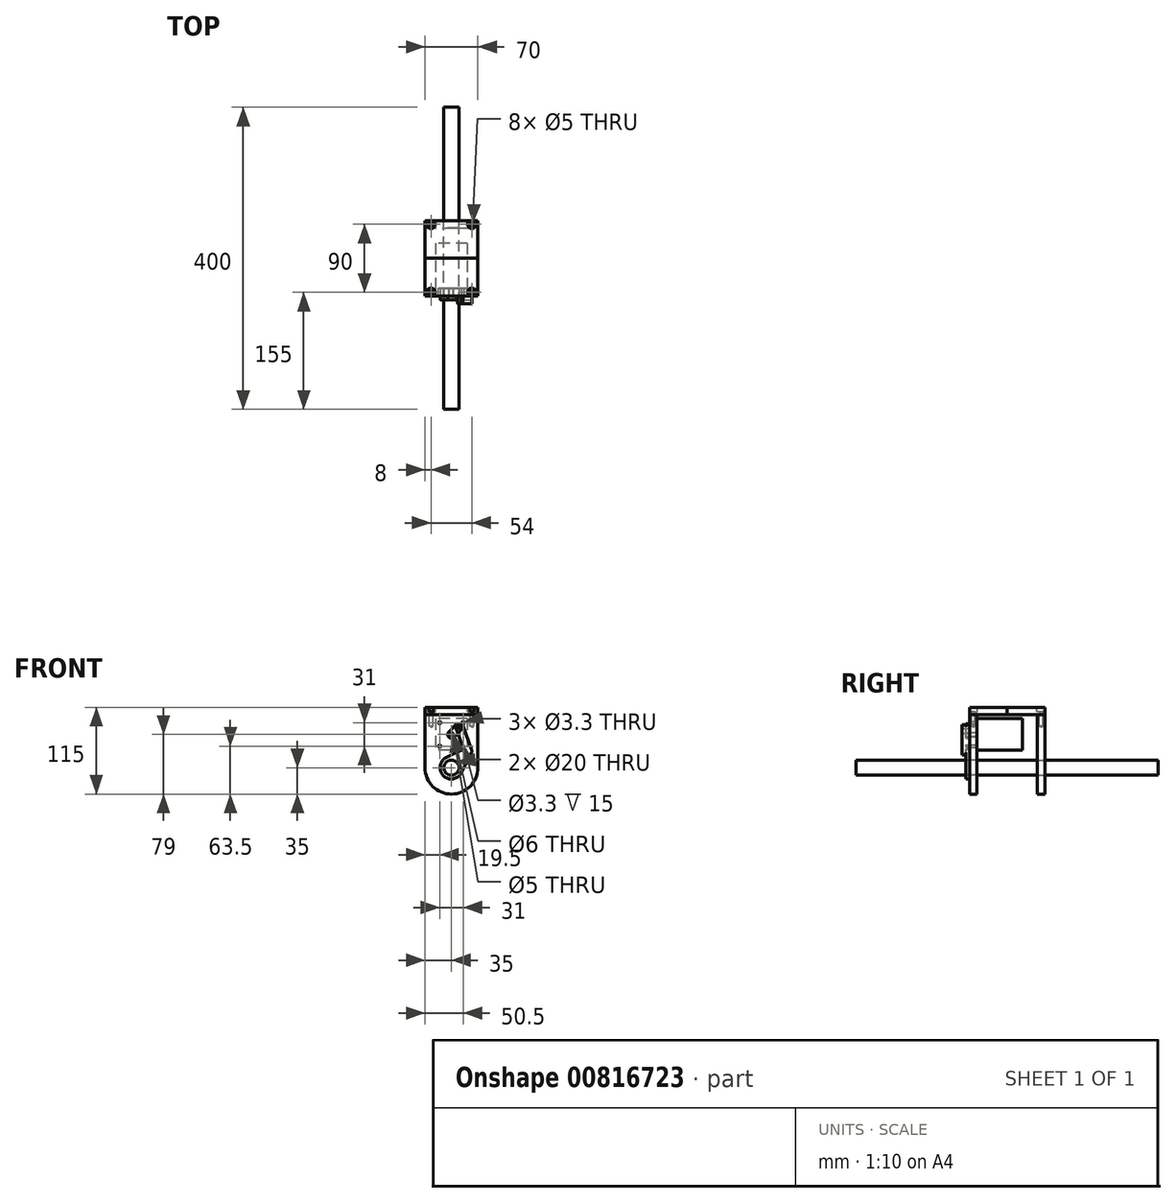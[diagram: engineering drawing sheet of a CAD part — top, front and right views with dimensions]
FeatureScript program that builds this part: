
annotation { "Feature Type Name" : "Feature", "Feature Type Description" : "" }
export const myFeature = defineFeature(function(context is Context, id is Id, definition is map)
    precondition{}
    {
        {
            var Q0;
            Q0=qCreatedBy(makeId("Front.planeOp"),FACE);
            var sketch = newSketch(context, id + "F0", { "sketchPlane" : qUnion([Q0])});
            skCircle(sketch, "E0", {"center": v(0, 0) * mm, "radius": 10 * mm});
            skLineSegment(sketch, "E1.bottom", {"start": v(-35, 70) * mm, "end": v(35, 70) * mm});
            skLineSegment(sketch, "E1.left", {"start": v(-35, 70) * mm, "end": v(-35, 0) * mm});
            skLineSegment(sketch, "E1.right", {"start": v(35, 70) * mm, "end": v(35, 0) * mm});
            skArc(sketch, "E2", {"start": v(-35, 0) * mm, "mid": v(0, -35) * mm, "end": v(35, 0) * mm});
            skSolve(sketch);
        }
        {
            var Q0;
            Q0=makeQuery(id+"F0.imprint","IMPRINT",FACE,{"disambiguationData":[TD([[makeQuery(id+"F0.imprint","IMPRINT",EDGE,{"derivedFrom":sQuery(id+"F0.wireOp",EDGE,"E0")}),1.0]])]});
            extrude(context, id + "F1", {"entities" : qUnion([Q0]), "depth" : 200 * mm, "offsetDistance" : 25 * mm, "hasSecondDirection" : true, "secondDirectionOppositeDirection" : true, "secondDirectionDepth" : 200 * mm});
        }
        {
            var Q0;
            Q0=makeQuery(id+"F0.imprint","IMPRINT",FACE,{"disambiguationData":[TD([[makeQuery(id+"F0.imprint","IMPRINT",EDGE,{"derivedFrom":sQuery(id+"F0.wireOp",EDGE,"E0")}),-1.0]])]});
            extrude(context, id + "F2", {"entities" : qUnion([Q0]), "depth" : 10 * mm, "offsetDistance" : 25 * mm});
        }
        {
            var Q0;
            Q0=makeQuery(id+"F2.opExtrude","SWEPT_BODY",BODY,{"disambiguationData":[OSD([sQuery(id+"F0.wireOp",EDGE,"E0"),sQuery(id+"F0.wireOp",EDGE,"E1.bottom"),sQuery(id+"F0.wireOp",EDGE,"E1.left"),sQuery(id+"F0.wireOp",EDGE,"E1.right"),sQuery(id+"F0.wireOp",EDGE,"E2")])]});
            var Q1;
            Q1=makeQuery(id+"F1.opExtrude","SWEPT_FACE",FACE,{"disambiguationData":[OSD([sQuery(id+"F0.wireOp",EDGE,"E0")])]});
            transform(context, id + "F3", {"entities" : qUnion([Q0]), "transformType" : TransformType.TRANSLATION_DISTANCE, "transformDirection" : qUnion([Q1]), "distance" : 50 * mm, "makeCopy" : false});
        }
        {
            var Q0;
            Q0=makeQuery(id+"F2.opExtrude","SWEPT_FACE",FACE,{"disambiguationData":[OSD([sQuery(id+"F0.wireOp",EDGE,"E1.bottom")])]});
            var sketch = newSketch(context, id + "F4", { "sketchPlane" : qUnion([Q0])});
            skPoint(sketch, "E3", {"position": v(27, 45) * mm});
            skPoint(sketch, "E3.positionSnap0", {"position": v(35, 45) * mm});
            skPoint(sketch, "E4", {"position": v(-27, 45) * mm});
            skPoint(sketch, "E4.positionSnap0", {"position": v(-35, 45) * mm});
            skSolve(sketch);
        }
        {
            var Q0;
            Q0=sQuery(id+"F4.wireOp",VERTEX,"E3");
            var Q1;
            Q1=sQuery(id+"F4.wireOp",VERTEX,"E4");
            var Q2;
            Q2=makeQuery(id+"F2.opExtrude","SWEPT_BODY",BODY,{"disambiguationData":[OSD([sQuery(id+"F0.wireOp",EDGE,"E0"),sQuery(id+"F0.wireOp",EDGE,"E1.bottom"),sQuery(id+"F0.wireOp",EDGE,"E1.left"),sQuery(id+"F0.wireOp",EDGE,"E1.right"),sQuery(id+"F0.wireOp",EDGE,"E2")])]});
            hole(context, id + "F5", {"style" : HoleStyle.SIMPLE, "endStyle" : HoleEndStyle.BLIND, "standardTappedOrClearance" : lookupTablePath({ "standard" : "ISO", "engagement" : "75%", "pitch" : "1 mm", "size" : "M6", "type" : "Tapped" }), "standardBlindInLast" : lookupTablePath({ "standard" : "ISO", "engagement" : "75%", "pitch" : "1 mm", "size" : "M6", "type" : "Tapped" }), "holeDiameter" : 5 * mm, "majorDiameter" : 6 * mm, "showTappedDepth" : true, "holeDepth" : 15 * mm, "isTappedThrough" : true, "tappedDepth" : 12 * mm, "tapClearance" : 3, "locations" : qUnion([Q0, Q1]), "scope" : qUnion([Q2])});
        }
        {
            var Q0;
            Q0=makeQuery(id+"F2.opExtrude","SWEPT_FACE",FACE,{"disambiguationData":[OSD([sQuery(id+"F0.wireOp",EDGE,"E1.bottom")])]});
            var sketch = newSketch(context, id + "F6", { "sketchPlane" : qUnion([Q0])});
            skLineSegment(sketch, "E5.bottom", {"start": v(-35, 50) * mm, "end": v(35, 50) * mm});
            skLineSegment(sketch, "E5.top", {"start": v(-35, 0) * mm, "end": v(35, 0) * mm});
            skLineSegment(sketch, "E5.left", {"start": v(-35, 50) * mm, "end": v(-35, 0) * mm});
            skLineSegment(sketch, "E5.right", {"start": v(35, 50) * mm, "end": v(35, 0) * mm});
            skPoint(sketch, "E6", {"position": v(0, 50) * mm});
            skPoint(sketch, "E7.centerSnap0", {"position": v(-35, 45) * mm});
            skPoint(sketch, "E8.centerSnap0", {"position": v(35, 45) * mm});
            skSolve(sketch);
        }
        {
            var Q0;
            {var subQ1=sQuery(id+"F0.wireOp",EDGE,"E1.bottom");Q0=makeQuery(id+"F6.imprint","IMPRINT",FACE,{"disambiguationData":[TD([[makeQuery(id+"F6.imprint","IMPRINT",EDGE,{"derivedFrom":makeQuery(id+"F2.opExtrude","CAP_EDGE",EDGE,{"disambiguationData":[OSD([subQ1])],"isStart":false})}),1.0]])]});}
            var Q1;
            Q1=makeQuery(id+"F6.imprint","IMPRINT",FACE,{"disambiguationData":[TD([[makeQuery(id+"F6.imprint","IMPRINT",EDGE,{"derivedFrom":sQuery(id+"F6.wireOp",EDGE,"E5.top")}),1.0]])]});
            extrude(context, id + "F7", {"entities" : qUnion([Q0, Q1]), "depth" : 10 * mm, "offsetDistance" : 25 * mm});
        }
        {
            var Q0;
            Q0=makeQuery(id+"F7.opExtrude","CAP_FACE",FACE,{"disambiguationData":[OSD([sQuery(id+"F5.hole-0.sketch.wireOp",EDGE,"core_line_2"),sQuery(id+"F5.hole-0.sketch.wireOp",EDGE,"core_line_3"),sQuery(id+"F5.hole-1.sketch.wireOp",EDGE,"core_line_2"),sQuery(id+"F5.hole-1.sketch.wireOp",EDGE,"core_line_3"),sQuery(id+"F6.wireOp",EDGE,"E5.bottom"),sQuery(id+"F6.wireOp",EDGE,"E5.top"),sQuery(id+"F6.wireOp",EDGE,"E5.left"),sQuery(id+"F6.wireOp",EDGE,"E5.right")])],"isStart":false});
            var sketch = newSketch(context, id + "F8", { "sketchPlane" : qUnion([Q0])});
            skPoint(sketch, "E9", {"position": v(27, 45) * mm});
            skPoint(sketch, "E10", {"position": v(-27, 45) * mm});
            skSolve(sketch);
        }
        {
            var Q0;
            Q0=sQuery(id+"F8.wireOp",VERTEX,"E9");
            var Q1;
            Q1=sQuery(id+"F8.wireOp",VERTEX,"E10");
            var Q2;
            Q2=makeQuery(id+"F7.opExtrude","SWEPT_BODY",BODY,{"disambiguationData":[OSD([sQuery(id+"F5.hole-0.sketch.wireOp",EDGE,"core_line_2"),sQuery(id+"F5.hole-0.sketch.wireOp",EDGE,"core_line_3"),sQuery(id+"F5.hole-1.sketch.wireOp",EDGE,"core_line_2"),sQuery(id+"F5.hole-1.sketch.wireOp",EDGE,"core_line_3"),sQuery(id+"F6.wireOp",EDGE,"E5.bottom"),sQuery(id+"F6.wireOp",EDGE,"E5.top"),sQuery(id+"F6.wireOp",EDGE,"E5.left"),sQuery(id+"F6.wireOp",EDGE,"E5.right")])]});
            hole(context, id + "F9", {"style" : HoleStyle.C_BORE, "endStyle" : HoleEndStyle.BLIND, "standardTappedOrClearance" : lookupTablePath({ "standard" : "ISO", "engagement" : "75%", "pitch" : "1 mm", "size" : "M6", "type" : "Tapped" }), "standardBlindInLast" : lookupTablePath({ "standard" : "ISO", "engagement" : "75%", "pitch" : "1 mm", "size" : "M6", "type" : "Tapped" }), "holeDiameter" : 5 * mm, "cBoreDiameter" : 11.25 * mm, "cBoreDepth" : 6 * mm, "majorDiameter" : 6 * mm, "showTappedDepth" : true, "holeDepth" : 15 * mm, "isTappedThrough" : true, "tappedDepth" : 12 * mm, "tapClearance" : 3, "locations" : qUnion([Q0, Q1]), "scope" : qUnion([Q2])});
        }
        {
            var Q0;
            Q0=makeQuery(id+"F2.opExtrude","SWEPT_BODY",BODY,{"disambiguationData":[OSD([sQuery(id+"F0.wireOp",EDGE,"E0"),sQuery(id+"F0.wireOp",EDGE,"E1.bottom"),sQuery(id+"F0.wireOp",EDGE,"E1.left"),sQuery(id+"F0.wireOp",EDGE,"E1.right"),sQuery(id+"F0.wireOp",EDGE,"E2")])]});
            var Q1;
            Q1=makeQuery(id+"F7.opExtrude","SWEPT_BODY",BODY,{"disambiguationData":[OSD([sQuery(id+"F5.hole-0.sketch.wireOp",EDGE,"core_line_2"),sQuery(id+"F5.hole-0.sketch.wireOp",EDGE,"core_line_3"),sQuery(id+"F5.hole-1.sketch.wireOp",EDGE,"core_line_2"),sQuery(id+"F5.hole-1.sketch.wireOp",EDGE,"core_line_3"),sQuery(id+"F6.wireOp",EDGE,"E5.bottom"),sQuery(id+"F6.wireOp",EDGE,"E5.top"),sQuery(id+"F6.wireOp",EDGE,"E5.left"),sQuery(id+"F6.wireOp",EDGE,"E5.right")])]});
            var Q2;
            Q2=qCreatedBy(makeId("Front.planeOp"),FACE);
            mirror(context, id + "F10", {"entities" : qUnion([Q0, Q1]), "mirrorPlane" : qUnion([Q2])});
        }
        {
            var Q0;
            Q0=makeQuery(id+"F10.opPattern","COPY",FACE,{"derivedFrom":makeQuery(id+"F2.opExtrude","CAP_FACE",FACE,{"disambiguationData":[OSD([sQuery(id+"F0.wireOp",EDGE,"E0"),sQuery(id+"F0.wireOp",EDGE,"E1.bottom"),sQuery(id+"F0.wireOp",EDGE,"E1.left"),sQuery(id+"F0.wireOp",EDGE,"E1.right"),sQuery(id+"F0.wireOp",EDGE,"E2")])],"isStart":false}),"instanceName":"1"});
            var sketch = newSketch(context, id + "F11", { "sketchPlane" : qUnion([Q0])});
            skLineSegment(sketch, "E11.bottom", {"start": v(-21, 65) * mm, "end": v(21, 65) * mm});
            skLineSegment(sketch, "E11.top", {"start": v(-21, 23) * mm, "end": v(21, 23) * mm});
            skLineSegment(sketch, "E11.left", {"start": v(-21, 65) * mm, "end": v(-21, 23) * mm});
            skLineSegment(sketch, "E11.right", {"start": v(21, 65) * mm, "end": v(21, 23) * mm});
            skPoint(sketch, "E12", {"position": v(0, 65) * mm});
            skPoint(sketch, "E13", {"position": v(-15.5, 59.5) * mm});
            skPoint(sketch, "E14.0.1.0", {"position": v(-15.5, 28.5) * mm});
            skPoint(sketch, "E14.1.0.0", {"position": v(15.5, 59.5) * mm});
            skPoint(sketch, "E14.1.1.0", {"position": v(15.5, 28.5) * mm});
            skLineSegment(sketch, "E14.direction1", {"start": v(-15.5, 59.5) * mm, "end": v(15.5, 59.5) * mm, "construction": true});
            skLineSegment(sketch, "E14.direction2", {"start": v(-15.5, 59.5) * mm, "end": v(-15.5, 28.5) * mm, "construction": true});
            skCircle(sketch, "E15", {"center": v(0, 44) * mm, "radius": 3 * mm});
            skPoint(sketch, "E15.centerSnap0", {"position": v(-21, 44) * mm});
            skPoint(sketch, "E15.centerSnap1", {"position": v(0, 23) * mm});
            skCircle(sketch, "E16", {"center": v(0, 44) * mm, "radius": 2.5 * mm});
            skSolve(sketch);
        }
        {
            var Q0;
            Q0=sQuery(id+"F11.wireOp",VERTEX,"E13");
            var Q1;
            Q1=sQuery(id+"F11.wireOp",VERTEX,"E14.0.1.0");
            var Q2;
            Q2=sQuery(id+"F11.wireOp",VERTEX,"E14.1.1.0");
            var Q3;
            Q3=sQuery(id+"F11.wireOp",VERTEX,"E14.1.0.0");
            var Q4;
            Q4=makeQuery(id+"F10.opPattern","COPY",BODY,{"derivedFrom":makeQuery(id+"F2.opExtrude","SWEPT_BODY",BODY,{"disambiguationData":[OSD([sQuery(id+"F0.wireOp",EDGE,"E0"),sQuery(id+"F0.wireOp",EDGE,"E1.bottom"),sQuery(id+"F0.wireOp",EDGE,"E1.left"),sQuery(id+"F0.wireOp",EDGE,"E1.right"),sQuery(id+"F0.wireOp",EDGE,"E2")])]}),"instanceName":"1"});
            hole(context, id + "F12", {"style" : HoleStyle.SIMPLE, "endStyle" : HoleEndStyle.THROUGH, "standardTappedOrClearance" : lookupTablePath({ "standard" : "ISO", "fit" : "Normal", "size" : "M3", "type" : "Clearance" }), "standardBlindInLast" : lookupTablePath({ "fit" : "Standard", "standard" : "ISO", "size" : "M3", "type" : "Clearance" }), "holeDiameter" : 3.3 * mm, "majorDiameter" : 6 * mm, "isTappedThrough" : true, "tappedDepth" : 12 * mm, "tapClearance" : 3, "locations" : qUnion([Q0, Q1, Q2, Q3]), "scope" : qUnion([Q4])});
        }
        {
            var Q0;
            Q0=makeQuery(id+"F11.imprint","IMPRINT",FACE,{"disambiguationData":[TD([[makeQuery(id+"F11.imprint","IMPRINT",EDGE,{"derivedFrom":sQuery(id+"F11.wireOp",EDGE,"E11.bottom")}),-1.0]])]});
            var Q1;
            Q1=makeQuery(id+"F11.imprint","IMPRINT",FACE,{"disambiguationData":[TD([[makeQuery(id+"F11.imprint","IMPRINT",EDGE,{"derivedFrom":sQuery(id+"F11.wireOp",EDGE,"E15")}),1.0]])]});
            var Q2;
            Q2=makeQuery(id+"F11.imprint","IMPRINT",FACE,{"disambiguationData":[TD([[makeQuery(id+"F11.imprint","IMPRINT",EDGE,{"derivedFrom":sQuery(id+"F11.wireOp",EDGE,"E16")}),1.0]])]});
            extrude(context, id + "F13", {"entities" : qUnion([Q0, Q1, Q2]), "depth" : 60 * mm, "offsetDistance" : 25 * mm});
        }
        {
            var Q0;
            Q0=makeQuery(id+"F11.imprint","IMPRINT",FACE,{"disambiguationData":[TD([[makeQuery(id+"F11.imprint","IMPRINT",EDGE,{"derivedFrom":sQuery(id+"F11.wireOp",EDGE,"E16")}),1.0]])]});
            var Q1;
            Q1=makeQuery(id+"F11.imprint","IMPRINT",FACE,{"disambiguationData":[TD([[makeQuery(id+"F11.imprint","IMPRINT",EDGE,{"derivedFrom":sQuery(id+"F11.wireOp",EDGE,"E15")}),1.0]])]});
            var Q2;
            Q2=makeQuery(id+"F10.opPattern","COPY",FACE,{"derivedFrom":makeQuery(id+"F2.opExtrude","CAP_FACE",FACE,{"disambiguationData":[OSD([sQuery(id+"F0.wireOp",EDGE,"E0"),sQuery(id+"F0.wireOp",EDGE,"E1.bottom"),sQuery(id+"F0.wireOp",EDGE,"E1.left"),sQuery(id+"F0.wireOp",EDGE,"E1.right"),sQuery(id+"F0.wireOp",EDGE,"E2")])],"isStart":true}),"instanceName":"1"});
            extrude(context, id + "F14", {"entities" : qUnion([Q0, Q1]), "operationType" : NewBodyOperationType.REMOVE, "endBound" : BoundingType.UP_TO_SURFACE, "oppositeDirection" : true, "depth" : 25 * mm, "endBoundEntityFace" : qUnion([Q2]), "offsetDistance" : 25 * mm});
        }
        {
            var Q0;
            Q0=makeQuery(id+"F11.imprint","IMPRINT",FACE,{"disambiguationData":[TD([[makeQuery(id+"F11.imprint","IMPRINT",EDGE,{"derivedFrom":sQuery(id+"F11.wireOp",EDGE,"E16")}),1.0]])]});
            extrude(context, id + "F15", {"entities" : qUnion([Q0]), "operationType" : NewBodyOperationType.ADD, "oppositeDirection" : true, "depth" : 15 * mm, "offsetDistance" : 25 * mm});
        }
        {
            var Q0;
            Q0=makeQuery(id+"F10.opPattern","COPY",FACE,{"derivedFrom":makeQuery(id+"F2.opExtrude","CAP_FACE",FACE,{"disambiguationData":[OSD([sQuery(id+"F0.wireOp",EDGE,"E0"),sQuery(id+"F0.wireOp",EDGE,"E1.bottom"),sQuery(id+"F0.wireOp",EDGE,"E1.left"),sQuery(id+"F0.wireOp",EDGE,"E1.right"),sQuery(id+"F0.wireOp",EDGE,"E2")])],"isStart":true}),"instanceName":"1"});
            var sketch = newSketch(context, id + "F16", { "sketchPlane" : qUnion([Q0])});
            skLineSegment(sketch, "E17", {"start": v(-6.63, 13.45) * mm, "end": v(19.79, 26.48) * mm});
            skLineSegment(sketch, "E18", {"start": v(13.45, -6.63) * mm, "end": v(26.48, 19.79) * mm});
            skArc(sketch, "E19", {"start": v(19.79, 26.48) * mm, "mid": v(25.54, 25.54) * mm, "end": v(26.48, 19.79) * mm});
            skArc(sketch, "E20", {"start": v(-6.63, 13.45) * mm, "mid": v(-10.6, -10.6) * mm, "end": v(13.45, -6.63) * mm});
            skLineSegment(sketch, "E21", {"start": v(-3.54, 47.54) * mm, "end": v(7.07, 58.14) * mm});
            skLineSegment(sketch, "E22", {"start": v(3.54, 40.46) * mm, "end": v(14.14, 51.07) * mm});
            skArc(sketch, "E23", {"start": v(-3.54, 47.54) * mm, "mid": v(-3.54, 40.46) * mm, "end": v(3.54, 40.46) * mm});
            skArc(sketch, "E24", {"start": v(7.07, 58.14) * mm, "mid": v(14.14, 58.14) * mm, "end": v(14.14, 51.07) * mm});
            skLineSegment(sketch, "E25", {"start": v(0, 0) * mm, "end": v(22, 22) * mm, "construction": true});
            skCircle(sketch, "E26", {"center": v(10.6, 54.6) * mm, "radius": 2.5 * mm});
            skCircle(sketch, "E27", {"center": v(22, 22) * mm, "radius": 2.5 * mm});
            skCircle(sketch, "E28", {"center": v(0, 44) * mm, "radius": 2.5 * mm});
            skLineSegment(sketch, "E29", {"start": v(15.33, 56.26) * mm, "end": v(26.72, 23.65) * mm});
            skLineSegment(sketch, "E30", {"start": v(5.89, 52.96) * mm, "end": v(17.28, 20.35) * mm});
            skArc(sketch, "E31", {"start": v(26.72, 23.65) * mm, "mid": v(23.65, 17.28) * mm, "end": v(17.28, 20.35) * mm});
            skArc(sketch, "E32", {"start": v(15.33, 56.26) * mm, "mid": v(8.96, 59.33) * mm, "end": v(5.89, 52.96) * mm});
            skLineSegment(sketch, "E33", {"start": v(0, 44) * mm, "end": v(22, 22) * mm, "construction": true});
            skLineSegment(sketch, "E34", {"start": v(0, 44) * mm, "end": v(10.6, 54.6) * mm, "construction": true});
            skSolve(sketch);
        }
        {
            var Q0;
            {var subQ0=sQuery(id+"F16.wireOp",EDGE,"E17");var subQ1=makeQuery(id+"F12.hole-1.boolean.opBoolean","INTERSECT",EDGE,{"derivedFrom":[makeQuery(id+"F10.opPattern","COPY",FACE,{"derivedFrom":makeQuery(id+"F2.opExtrude","CAP_FACE",FACE,{"disambiguationData":[OSD([sQuery(id+"F0.wireOp",EDGE,"E0"),sQuery(id+"F0.wireOp",EDGE,"E1.bottom"),sQuery(id+"F0.wireOp",EDGE,"E1.left"),sQuery(id+"F0.wireOp",EDGE,"E1.right"),sQuery(id+"F0.wireOp",EDGE,"E2")])],"isStart":true}),"instanceName":"1"}),makeQuery(id+"F12.hole-1.opRevolve","SWEPT_FACE",FACE,{"disambiguationData":[OSD([sQuery(id+"F12.hole-1.sketch.wireOp",EDGE,"core_line_2")])]})]});var subQ2=makeQuery(id+"F16.imprint","INTERSECT",VERTEX,{"disambiguationData":[OD(0.0)],"derivedFrom":[subQ1,subQ0]});Q0=makeQuery(id+"F16.imprint","IMPRINT",FACE,{"disambiguationData":[TD([[makeQuery(id+"F16.imprint","IMPRINT",EDGE,{"disambiguationData":[TD([[subQ2,-1.0]])],"derivedFrom":subQ0}),-1.0]])]});}
            var Q1;
            Q1=makeQuery(id+"F16.imprint","IMPRINT",FACE,{"disambiguationData":[TD([[makeQuery(id+"F16.imprint","IMPRINT",EDGE,{"derivedFrom":sQuery(id+"F16.wireOp",EDGE,"E28")}),-1.0]])]});
            var Q2;
            {var subQ6=sQuery(id+"F16.wireOp",EDGE,"E21");Q2=makeQuery(id+"F16.imprint","IMPRINT",FACE,{"disambiguationData":[TD([[makeQuery(id+"F16.imprint","IMPRINT",EDGE,{"derivedFrom":subQ6}),-1.0]])]});}
            var Q3;
            {var subQ1=sQuery(id+"F16.wireOp",EDGE,"E18");Q3=makeQuery(id+"F16.imprint","IMPRINT",FACE,{"disambiguationData":[TD([[makeQuery(id+"F16.imprint","IMPRINT",EDGE,{"derivedFrom":subQ1}),1.0]])]});}
            var Q4;
            {var subQ5=sQuery(id+"F16.wireOp",EDGE,"E24");Q4=makeQuery(id+"F16.imprint","IMPRINT",FACE,{"disambiguationData":[TD([[makeQuery(id+"F16.imprint","IMPRINT",EDGE,{"derivedFrom":subQ5}),-1.0]])]});}
            var Q5;
            {var subQ0=sQuery(id+"F16.wireOp",EDGE,"E19");Q5=makeQuery(id+"F16.imprint","IMPRINT",FACE,{"disambiguationData":[TD([[makeQuery(id+"F16.imprint","IMPRINT",EDGE,{"derivedFrom":subQ0}),-1.0]])]});}
            extrude(context, id + "F17", {"entities" : qUnion([Q0, Q1, Q2, Q3, Q4, Q5]), "depth" : 5 * mm, "offsetDistance" : 25 * mm});
        }
        {
            var Q0;
            {var subQ0=sQuery(id+"F16.wireOp",EDGE,"E30");var subQ1=makeQuery(id+"F12.hole-1.boolean.opBoolean","INTERSECT",EDGE,{"derivedFrom":[makeQuery(id+"F10.opPattern","COPY",FACE,{"derivedFrom":makeQuery(id+"F2.opExtrude","CAP_FACE",FACE,{"disambiguationData":[OSD([sQuery(id+"F0.wireOp",EDGE,"E0"),sQuery(id+"F0.wireOp",EDGE,"E1.bottom"),sQuery(id+"F0.wireOp",EDGE,"E1.left"),sQuery(id+"F0.wireOp",EDGE,"E1.right"),sQuery(id+"F0.wireOp",EDGE,"E2")])],"isStart":true}),"instanceName":"1"}),makeQuery(id+"F12.hole-1.opRevolve","SWEPT_FACE",FACE,{"disambiguationData":[OSD([sQuery(id+"F12.hole-1.sketch.wireOp",EDGE,"core_line_2")])]})]});var subQ2=makeQuery(id+"F16.imprint","INTERSECT",VERTEX,{"disambiguationData":[OD(0.0)],"derivedFrom":[subQ1,subQ0]});Q0=makeQuery(id+"F16.imprint","IMPRINT",FACE,{"disambiguationData":[TD([[makeQuery(id+"F16.imprint","IMPRINT",EDGE,{"disambiguationData":[TD([[subQ2,-1.0]])],"derivedFrom":subQ0}),1.0]])]});}
            var Q1;
            {var subQ4=sQuery(id+"F16.wireOp",EDGE,"E19");Q1=makeQuery(id+"F16.imprint","IMPRINT",FACE,{"disambiguationData":[TD([[makeQuery(id+"F16.imprint","IMPRINT",EDGE,{"derivedFrom":subQ4}),1.0]])]});}
            var Q2;
            {var subQ2=sQuery(id+"F16.wireOp",EDGE,"E24");Q2=makeQuery(id+"F16.imprint","IMPRINT",FACE,{"disambiguationData":[TD([[makeQuery(id+"F16.imprint","IMPRINT",EDGE,{"derivedFrom":subQ2}),-1.0]])]});}
            var Q3;
            {var subQ5=sQuery(id+"F16.wireOp",EDGE,"E19");Q3=makeQuery(id+"F16.imprint","IMPRINT",FACE,{"disambiguationData":[TD([[makeQuery(id+"F16.imprint","IMPRINT",EDGE,{"derivedFrom":subQ5}),-1.0]])]});}
            extrude(context, id + "F18", {"entities" : qUnion([Q0, Q1, Q2, Q3]), "depth" : 10 * mm, "offsetDistance" : 25 * mm, "hasSecondDirection" : true, "secondDirectionOppositeDirection" : false, "secondDirectionDepth" : 5 * mm});
        }
        {
            var Q0;
            Q0=makeQuery(id+"F16.imprint","IMPRINT",FACE,{"disambiguationData":[TD([[makeQuery(id+"F16.imprint","IMPRINT",EDGE,{"derivedFrom":sQuery(id+"F16.wireOp",EDGE,"E26")}),1.0]])]});
            var Q1;
            Q1=makeQuery(id+"F16.imprint","IMPRINT",FACE,{"disambiguationData":[TD([[makeQuery(id+"F16.imprint","IMPRINT",EDGE,{"derivedFrom":sQuery(id+"F16.wireOp",EDGE,"E27")}),1.0]])]});
            var Q2;
            Q2=sQuery(id+"F16.wireOp",EDGE,"E26");
            var Q3;
            Q3=sQuery(id+"F16.wireOp",EDGE,"E27");
            extrude(context, id + "F19", {"entities" : qUnion([Q0, Q1]), "operationType" : NewBodyOperationType.ADD, "surfaceEntities" : qUnion([Q2, Q3]), "depth" : 10 * mm, "offsetDistance" : 25 * mm});
        }
    });
